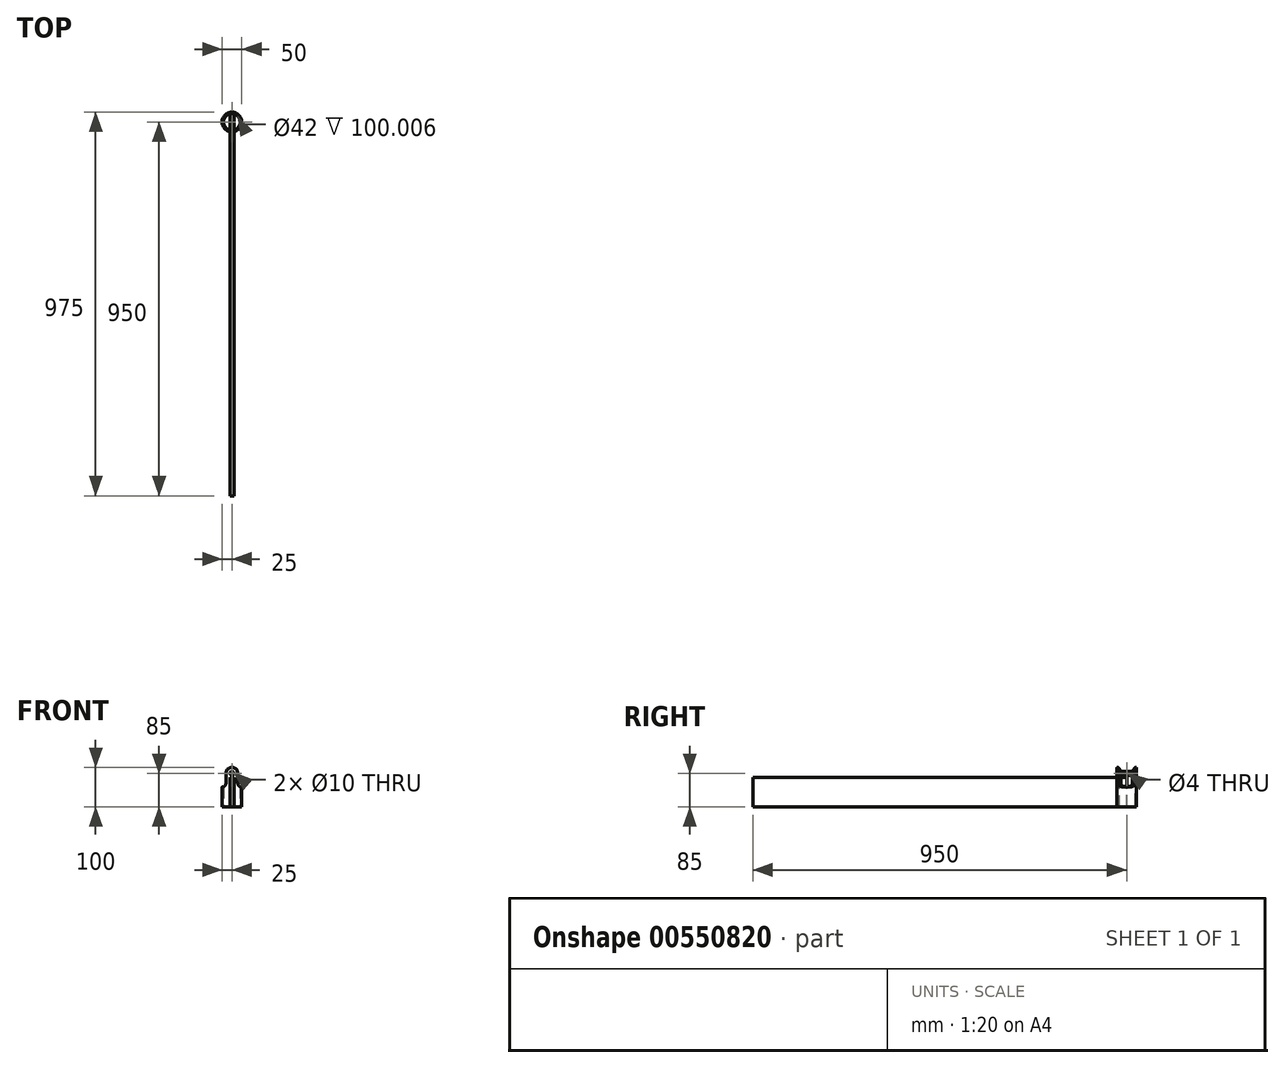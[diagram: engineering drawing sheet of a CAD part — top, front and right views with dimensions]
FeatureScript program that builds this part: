
annotation { "Feature Type Name" : "Feature", "Feature Type Description" : "" }
export const myFeature = defineFeature(function(context is Context, id is Id, definition is map)
    precondition{}
    {
        {
            var Q0;
            Q0=qCreatedBy(makeId("Top.planeOp"),FACE);
            var sketch = newSketch(context, id + "F0", { "sketchPlane" : qUnion([Q0])});
            skCircle(sketch, "E0", {"center": v(0, 0) * mm, "radius": 21 * mm});
            skCircle(sketch, "E1.0", {"center": v(0, 0) * mm, "radius": 25 * mm});
            skSolve(sketch);
        }
        {
            var Q0;
            Q0=makeQuery(id+"F0.imprint","IMPRINT",FACE,{"disambiguationData":[TD([[makeQuery(id+"F0.imprint","IMPRINT",EDGE,{"derivedFrom":sQuery(id+"F0.wireOp",EDGE,"E0")}),-1.0]])]});
            extrude(context, id + "F1", {"entities" : qUnion([Q0]), "depth" : 100 * mm, "offsetDistance" : 25 * mm});
        }
        {
            var Q0;
            Q0=qCreatedBy(makeId("Front.planeOp"),FACE);
            var sketch = newSketch(context, id + "F2", { "sketchPlane" : qUnion([Q0])});
            skLineSegment(sketch, "E2", {"start": v(-25, 50.21) * mm, "end": v(-25, 100) * mm});
            skLineSegment(sketch, "E3.0", {"start": v(-15, 60.21) * mm, "end": v(-15, 85) * mm});
            skLineSegment(sketch, "E4", {"start": v(0, 100) * mm, "end": v(0, 100) * mm});
            skLineSegment(sketch, "E5.0", {"start": v(-25, 50.21) * mm, "end": v(-25, 50.21) * mm});
            skArc(sketch, "E6.filletArc", {"start": v(-25, 50.21) * mm, "mid": v(-17.93, 53.14) * mm, "end": v(-15, 60.21) * mm});
            skArc(sketch, "E7.filletArc", {"start": v(0, 100) * mm, "mid": v(-10.6, 95.6) * mm, "end": v(-15, 85) * mm});
            skLineSegment(sketch, "E8", {"start": v(-25, 100) * mm, "end": v(0, 100) * mm});
            skLineSegment(sketch, "E9.MirrorCS", {"start": v(25, 100) * mm, "end": v(0, 100) * mm});
            skArc(sketch, "E10.MirrorCS", {"start": v(0, 100) * mm, "mid": v(10.6, 95.6) * mm, "end": v(15, 85) * mm});
            skLineSegment(sketch, "E11.MirrorCS", {"start": v(15, 60.21) * mm, "end": v(15, 85) * mm});
            skArc(sketch, "E12.MirrorCS", {"start": v(25, 50.21) * mm, "mid": v(17.93, 53.14) * mm, "end": v(15, 60.21) * mm});
            skLineSegment(sketch, "E13.MirrorCS", {"start": v(25, 50.21) * mm, "end": v(25, 100) * mm});
            skLineSegment(sketch, "E14.MirrorCS", {"start": v(25, 50.21) * mm, "end": v(25, 50.21) * mm});
            skSolve(sketch);
        }
        {
            var Q0;
            Q0 = qSketchRegion(id + "F2", true);
            extrude(context, id + "F3", {"entities" : qUnion([Q0]), "operationType" : NewBodyOperationType.REMOVE, "endBound" : BoundingType.SYMMETRIC, "oppositeDirection" : true, "depth" : 50 * mm, "offsetDistance" : 25 * mm});
        }
        {
            var Q0;
            Q0=qCreatedBy(makeId("Front.planeOp"),FACE);
            var sketch = newSketch(context, id + "F4", { "sketchPlane" : qUnion([Q0])});
            skCircle(sketch, "E15", {"center": v(0, 85) * mm, "radius": 5 * mm});
            skSolve(sketch);
        }
        {
            var Q0;
            Q0=makeQuery(id+"F4.imprint","IMPRINT",FACE,{"disambiguationData":[TD([[makeQuery(id+"F4.imprint","IMPRINT",EDGE,{"derivedFrom":sQuery(id+"F4.wireOp",EDGE,"E15")}),1.0]])]});
            var Q1;
            Q1=sQuery(id+"F4.wireOp",EDGE,"E15");
            extrude(context, id + "F5", {"entities" : qUnion([Q0]), "operationType" : NewBodyOperationType.REMOVE, "surfaceEntities" : qUnion([Q1]), "endBound" : BoundingType.SYMMETRIC, "oppositeDirection" : true, "depth" : 50 * mm, "offsetDistance" : 25 * mm});
        }
        {
            var Q0;
            Q0 = qSketchRegion(id + "F4", true);
            extrude(context, id + "F6", {"entities" : qUnion([Q0]), "endBound" : BoundingType.SYMMETRIC, "depth" : 50 * mm, "offsetDistance" : 25 * mm});
        }
        {
            var Q0;
            Q0=qCreatedBy(makeId("Right.planeOp"),FACE);
            var sketch = newSketch(context, id + "F7", { "sketchPlane" : qUnion([Q0])});
            skCircle(sketch, "E16", {"center": v(0, 85) * mm, "radius": 2 * mm});
            skSolve(sketch);
        }
        {
            var Q0;
            Q0 = qSketchRegion(id + "F7", true);
            extrude(context, id + "F8", {"entities" : qUnion([Q0]), "operationType" : NewBodyOperationType.REMOVE, "endBound" : BoundingType.SYMMETRIC, "oppositeDirection" : true, "depth" : 10 * mm, "offsetDistance" : 25 * mm});
        }
        {
            var Q0;
            Q0=qCreatedBy(makeId("Front.planeOp"),FACE);
            var sketch = newSketch(context, id + "F9", { "sketchPlane" : qUnion([Q0])});
            skLineSegment(sketch, "E17.0", {"start": v(5, 0) * mm, "end": v(5, 75) * mm});
            skLineSegment(sketch, "E18.0", {"start": v(-5, 0) * mm, "end": v(-5, 75) * mm});
            skLineSegment(sketch, "E19", {"start": v(-5, 75) * mm, "end": v(5, 75) * mm});
            skLineSegment(sketch, "E20", {"start": v(-5, 0) * mm, "end": v(5, 0) * mm});
            skSolve(sketch);
        }
        {
            var Q0;
            Q0 = qSketchRegion(id + "F9", true);
            extrude(context, id + "F10", {"entities" : qUnion([Q0]), "operationType" : NewBodyOperationType.ADD, "depth" : 950 * mm, "offsetDistance" : 25 * mm});
        }
    });
